# Revit family: Prises non verrouillées saillies 480_500V
name_source: partatom
category: Installations électriques
revit_build: Autodesk Revit 2018 (Build: 20170223_1515(x64)
units: mm (PartAtom-declared; Revit-internal decimal feet)

## family parameters
Conserver l'orientation des annotations = Non
Cote de connecteur circulaire = Utiliser le diamètre
Couper avec des vides une fois chargée = Non
Hôte = Face
Partagée = Non
Point de calcul de pièce = Non
Type d'élément = Normal

## types (8) — shared parameters
Couleur caractéristique = noir
Elévation par défaut = 1000 mm  [stored 3.28084 ft]
Fabricant = Legrand
Famille produit = 0854-P17 TEMPRA PRO
Position de la Terre h = 7
Prise au standard international pour montage encastré ou saillie avec accessoire permet la connexion d'appareils de puissance = Prise au standard international pour montage encastré ou saillie avec accessoire permet la connexion d'appareils de puissance
Standard CEI ou NFC = CEI
Température maximum d'utilisation = 40
Température minimum d'installation = -5
Température minimum d'utilisation = -25
Tension V = 500 V  50/60 Hz  noir
Type de cerrouillage = x
matériau du boitier = plastique
résistance aux chocs IK = 9
type de raccordement = bornes à vis

## per-type parameters (varying)
| type | Description | Diamètre entrée de câble | Intensité A | Modèle | Nombre de pôles | classe de protection IP | entraxe de fixation horizontal mm | entraxe de fixation vertical mm | hauteur mm | largeur mm | profondeur mm | sans halogène |
| IDS_LG_555162 | IDS_DESCRIPTION_LG_555162 | M20/M25 | 16 A | LG-555162 | 4 | IP44 | 70 mm | 0 mm  [stored 0 ft] | 131 mm  [stored 0.42979 ft] | 93 mm | 133 mm  [stored 0.436352 ft] | Oui |
| IDS_LG_555163 | IDS_DESCRIPTION_LG_555163 | M20/M25 | 16 A | LG-555163 | 5 | IP44 | 70 mm | 0 mm  [stored 0 ft] | 131 mm  [stored 0.42979 ft] | 93 mm | 139 mm | Oui |
| IDS_LG_555262 | IDS_DESCRIPTION_LG_555262 | M25/M32 | 32 A | LG-555262 | 4 | IP44 | 90 mm | 0 mm  [stored 0 ft] | 156 mm  [stored 0.511811 ft] | 113 mm | 155 mm | Oui |
| IDS_LG_555263 | IDS_DESCRIPTION_LG_555263 | M25/M32 | 32 A | LG-555263 | 5 | IP44 | 90 mm | 0 mm  [stored 0 ft] | 156 mm  [stored 0.511811 ft] | 113 mm | 161 mm | Oui |
| IDS_LG_555362 | IDS_DESCRIPTION_LG_555362 | M20/M25 | 16 A | LG-555362 | 4 |  | 70 mm | 0 mm  [stored 0 ft] | 138 mm  [stored 0.452756 ft] | 93 mm | 134 mm  [stored 0.439633 ft] | Non |
| IDS_LG_555462 | IDS_DESCRIPTION_LG_555462 | M25/M32 | 32 A | LG-555462 | 4 |  | 90 mm | 0 mm  [stored 0 ft] | 163 mm  [stored 0.534777 ft] | 113 mm | 156 mm  [stored 0.511811 ft] | Non |
| IDS_LG_555463 | IDS_DESCRIPTION_LG_555463 | M25/M32 | 32 A | LG-555463 | 5 |  | 90 mm | 0 mm  [stored 0 ft] | 163 mm  [stored 0.534777 ft] | 113 mm | 162 mm | Non |
| IDS_LG_555562 | IDS_DESCRIPTION_LG_555562 | M32 | 63 A | LG-555562 | 4 |  | 119 mm | 156 mm  [stored 0.511811 ft] | 270 mm  [stored 0.885827 ft] | 130 mm | 190 mm | Non |

note: [stored X ft] marks values corroborated as IEEE doubles in the binary element streams (Revit-internal decimal feet)
